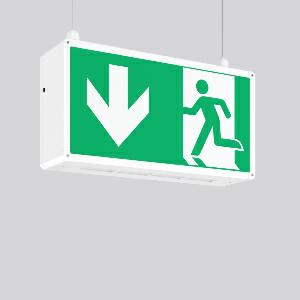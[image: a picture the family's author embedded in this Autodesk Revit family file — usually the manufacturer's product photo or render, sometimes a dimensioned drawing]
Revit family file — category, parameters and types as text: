
# Revit family: rechteck_seilpendel_671351_002_04_454b
name_source: partatom
category: Lighting Fixtures
units: mm (PartAtom-declared; Revit-internal decimal feet)

## family parameters
Cut with Voids When Loaded = No
Host = Face
Light Source = No
Part Type = Normal
Room Calculation Point = No
Round Connector Dimension = Use Diameter
Shared = No

## types (1)
- RECHTECK seilpendel
    Apparent Load = 0 VA
    Default Elevation = 1800 mm
    Description = Series: RECHTECK
Rectangular pendant luminaire in classic design. For escape route identification. Housing: aluminium, with plastic corner connectors. Display panels: plastic, opal, with motifs on one side/on both sides. Pendant luminaires (suspension provided on site) ready for connection to two suspension cables or chains. Driver integrated. Self-contained system with automatic self-test and feedback to the RZB monitoring system MULTIDIGIT. Please indicate legend number when placing your order! 
Colour: white
Length: 485 mm
Width: 125 mm
Height: 250 mm
Weight: 3.11 kg
Operating mode: maintained power mode
Viewing Distance: 43 m
Duration time: 3 h
Lamp: LED
Socket: without socket
Colour temperature: 6500K
Colour rendering index (CRI): 70
System power: 9.1 W
Control gear: Regulated power supply
Protection class: I
Type of protection: IP 44
    Height = 250 mm
    Lamp = 0 x
    Length = 485 mm
    Luminous efficacy = 0 lm/W
    Manufacturer = RZB
    ModVariant = No
    Model = 671351.002.04
    Mounting Place = Ceiling
    Mounting Type = Pendant
    Number of Poles = 1
    OnlyDefault = Yes
    Power Factor = 1
    Product Name = RECHTECK seilpendel
    Product group = Pendant luminaires
    ProductGroupID = 902
    Protection Class = Protection class I
    Protection Degree = IP 44
    RLX_Detail_Level = 1
    RLX_Emergency_Light_Flux = 0 lm
    RLX_Emergency_Type = 0
    RLX_Emergency_Type_DB = No
    RlxData = <blob elided: 57149 chars, md5=cb5b2fcf>
    Standby Power = 0 W
    System Light Flux = 0 lm
    System Power = 0 W
    Type Comments = Product without accessories
    Type Image = 671351.002.jpg
    URL = http://relux.com
    VarID = ---
    Voltage = 230 V
    Voltage Range = 220-240 V
    Weight = 0.00 kg
    Width = 125 mm

## geometry (parser evidence)
native form markers: Blend x4, Sweep x9
no freeform markers — native parametric forms only
